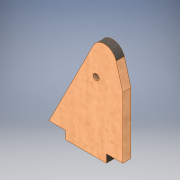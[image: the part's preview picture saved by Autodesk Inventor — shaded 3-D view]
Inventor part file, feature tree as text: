
AUTODESK INVENTOR PART (.ipt)
format: ipt  version: 2019 (Build 230136000, 136)  size: 133,120 bytes
history: native  units: mm
features: extrude x2, sketch x2, other x1
ambient origin geometry x8: Origin, YZ Plane, XZ Plane, XY Plane, X Axis, Y Axis, Z Axis, Center Point
bodies: Body1 (feature_tree)
feature tree (5):
  other  "Твердое тело1"
  extrude  "Выдавливание1"  Depth=6.0mm
  extrude  "Выдавливание2"  Depth=40.0mm
  sketch  "Эскиз1"
  sketch  "Эскиз2"
